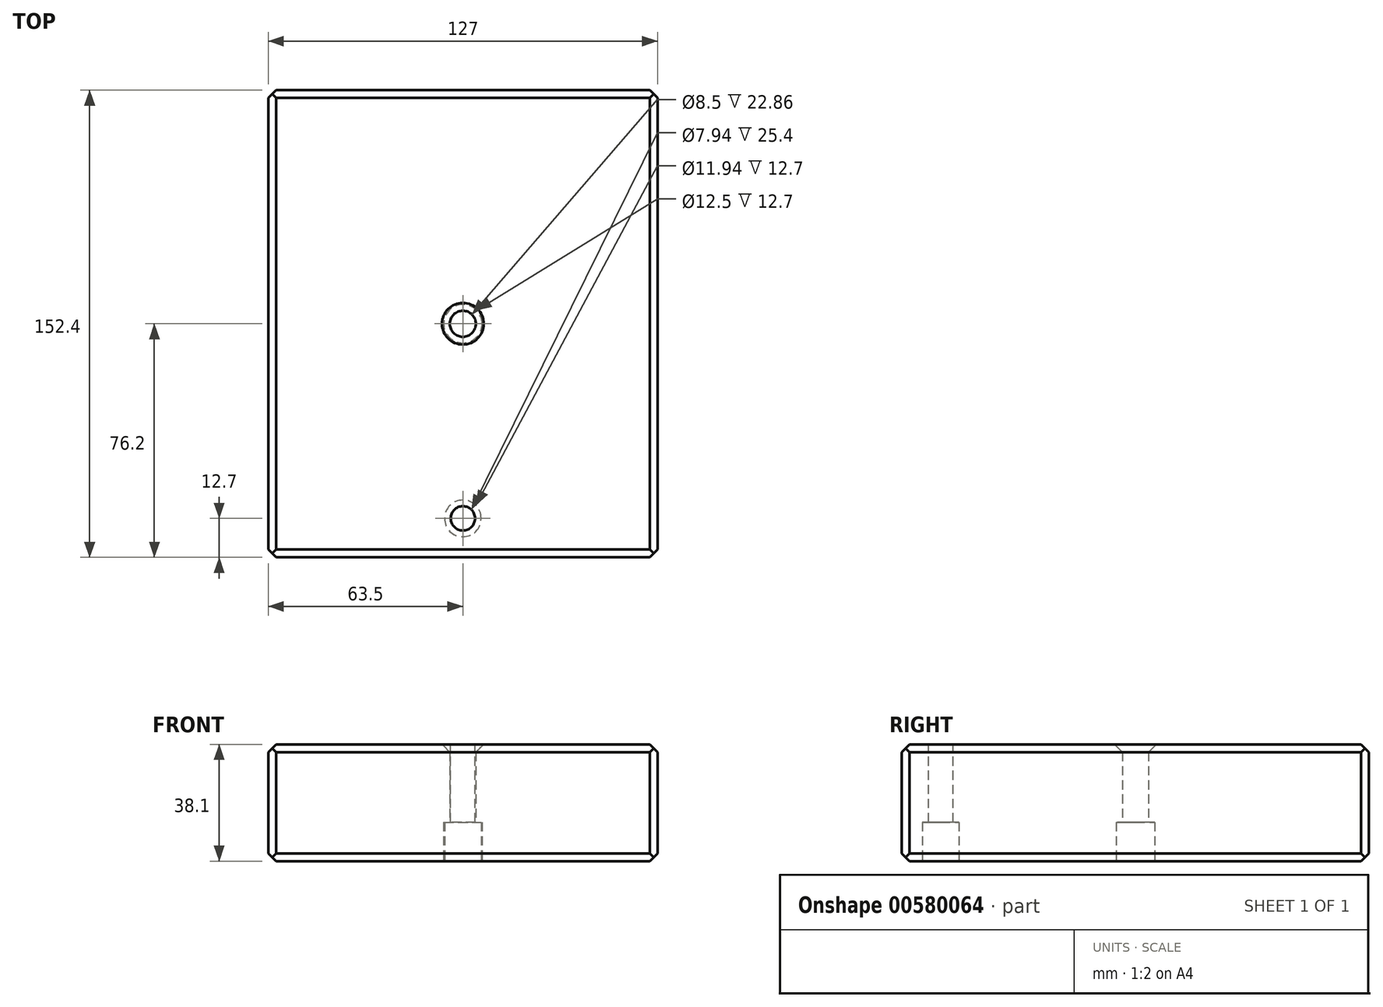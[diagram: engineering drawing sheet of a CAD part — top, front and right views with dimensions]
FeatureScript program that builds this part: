
annotation { "Feature Type Name" : "Feature", "Feature Type Description" : "" }
export const myFeature = defineFeature(function(context is Context, id is Id, definition is map)
    precondition{}
    {
        {
            var Q0;
            Q0=qCreatedBy(makeId("Top.planeOp"),FACE);
            var sketch = newSketch(context, id + "F0", { "sketchPlane" : qUnion([Q0])});
            skLineSegment(sketch, "E0.bottom", {"start": v(63.5, -76.2) * mm, "end": v(-63.5, -76.2) * mm});
            skLineSegment(sketch, "E0.top", {"start": v(63.5, 76.2) * mm, "end": v(-63.5, 76.2) * mm});
            skLineSegment(sketch, "E0.left", {"start": v(63.5, -76.2) * mm, "end": v(63.5, 76.2) * mm});
            skLineSegment(sketch, "E0.right", {"start": v(-63.5, -76.2) * mm, "end": v(-63.5, 76.2) * mm});
            skPoint(sketch, "E0.middle", {"position": v(0, 0) * mm});
            skCircle(sketch, "E1", {"center": v(0, 0) * mm, "radius": 4.25 * mm});
            skSolve(sketch);
        }
        {
            var Q0;
            Q0=makeQuery(id+"F0.imprint","IMPRINT",FACE,{"disambiguationData":[TD([[makeQuery(id+"F0.imprint","IMPRINT",EDGE,{"derivedFrom":sQuery(id+"F0.wireOp",EDGE,"E0.bottom")}),-1.0]])]});
            extrude(context, id + "F1", {"entities" : qUnion([Q0]), "depth" : 38.1 * mm, "offsetDistance" : 25.4 * mm});
        }
        {
            var Q0;
            Q0=makeQuery(id+"F1.opExtrude","CAP_FACE",FACE,{"disambiguationData":[OSD([sQuery(id+"F0.wireOp",EDGE,"E0.bottom"),sQuery(id+"F0.wireOp",EDGE,"E0.top"),sQuery(id+"F0.wireOp",EDGE,"E0.left"),sQuery(id+"F0.wireOp",EDGE,"E0.right"),sQuery(id+"F0.wireOp",EDGE,"E1")])],"isStart":false});
            var sketch = newSketch(context, id + "F2", { "sketchPlane" : qUnion([Q0])});
            skLineSegment(sketch, "E2", {"start": v(0, 94.71) * mm, "end": v(0, -95.69) * mm, "construction": true});
            skPoint(sketch, "E2.startSnap0", {"position": v(0, 76.2) * mm});
            skLineSegment(sketch, "E3", {"start": v(-99.6, 0) * mm, "end": v(96.99, 0) * mm, "construction": true});
            skSolve(sketch);
        }
        {
            var Q0;
            Q0=makeQuery(id+"F2.imprint","IMPRINT",FACE,{"disambiguationData":[TD([[makeQuery(id+"F2.imprint","IMPRINT",EDGE,{"derivedFrom":makeQuery(id+"F1.opExtrude","CAP_EDGE",EDGE,{"disambiguationData":[OSD([sQuery(id+"F0.wireOp",EDGE,"E0.bottom")])],"isStart":false})}),-1.0]])]});
            var sketch = newSketch(context, id + "F3", { "sketchPlane" : qUnion([Q0])});
            skCircle(sketch, "E4", {"center": v(0, -63.5) * mm, "radius": 3.97 * mm});
            skSolve(sketch);
        }
        {
            var Q0;
            Q0=makeQuery(id+"F3.imprint","IMPRINT",FACE,{"disambiguationData":[TD([[makeQuery(id+"F3.imprint","IMPRINT",EDGE,{"derivedFrom":sQuery(id+"F3.wireOp",EDGE,"E4")}),1.0]])]});
            var Q1;
            Q1=makeQuery(id+"F3.imprint","IMPRINT",FACE,{"disambiguationData":[TD([[makeQuery(id+"F3.imprint","IMPRINT",EDGE,{"derivedFrom":sQuery(id+"F3.wireOp",EDGE,"7c92b9c1-a204-463c-bf9a-26367c600006")}),1.0]])]});
            extrude(context, id + "F4", {"entities" : qUnion([Q0, Q1]), "operationType" : NewBodyOperationType.REMOVE, "oppositeDirection" : true, "depth" : 50.8 * mm, "offsetDistance" : 25.4 * mm});
        }
        {
            var Q0;
            Q0=makeQuery(id+"F1.opExtrude","CAP_FACE",FACE,{"disambiguationData":[OSD([sQuery(id+"F0.wireOp",EDGE,"E0.bottom"),sQuery(id+"F0.wireOp",EDGE,"E0.top"),sQuery(id+"F0.wireOp",EDGE,"E0.left"),sQuery(id+"F0.wireOp",EDGE,"E0.right"),sQuery(id+"F0.wireOp",EDGE,"E1")])],"isStart":true});
            var sketch = newSketch(context, id + "F5", { "sketchPlane" : qUnion([Q0])});
            skCircle(sketch, "E5.0", {"center": v(0, 63.5) * mm, "radius": 5.97 * mm});
            skCircle(sketch, "E6.0", {"center": v(0, 0) * mm, "radius": 6.25 * mm});
            skSolve(sketch);
        }
        {
            var Q0;
            Q0=makeQuery(id+"F5.imprint","IMPRINT",FACE,{"disambiguationData":[TD([[makeQuery(id+"F5.imprint","IMPRINT",EDGE,{"derivedFrom":sQuery(id+"F5.wireOp",EDGE,"E6.0")}),1.0]])]});
            var Q1;
            Q1=makeQuery(id+"F5.imprint","IMPRINT",FACE,{"disambiguationData":[TD([[makeQuery(id+"F5.imprint","IMPRINT",EDGE,{"derivedFrom":sQuery(id+"F5.wireOp",EDGE,"E5.0")}),1.0]])]});
            extrude(context, id + "F6", {"entities" : qUnion([Q0, Q1]), "operationType" : NewBodyOperationType.REMOVE, "oppositeDirection" : true, "depth" : 12.7 * mm, "offsetDistance" : 25.4 * mm});
        }
        {
            var Q0;
            Q0=makeQuery(id+"F6.boolean.opBoolean","COPY",EDGE,{"derivedFrom":makeQuery(id+"F6.opExtrude","CAP_EDGE",EDGE,{"disambiguationData":[OSD([sQuery(id+"F5.wireOp",EDGE,"E6.0")])],"isStart":true})});
            var Q1;
            Q1=makeQuery(id+"F4.boolean.opBoolean","INTERSECT",EDGE,{"derivedFrom":[makeQuery(id+"F1.opExtrude","CAP_FACE",FACE,{"disambiguationData":[OSD([sQuery(id+"F0.wireOp",EDGE,"E0.bottom"),sQuery(id+"F0.wireOp",EDGE,"E0.top"),sQuery(id+"F0.wireOp",EDGE,"E0.left"),sQuery(id+"F0.wireOp",EDGE,"E0.right"),sQuery(id+"F0.wireOp",EDGE,"E1")])],"isStart":true}),makeQuery(id+"F4.opExtrude","SWEPT_FACE",FACE,{"disambiguationData":[OSD([sQuery(id+"F3.wireOp",EDGE,"E4")])]})]});
            var Q2;
            Q2=makeQuery(id+"F6.boolean.opBoolean","COPY",EDGE,{"derivedFrom":makeQuery(id+"F6.opExtrude","CAP_EDGE",EDGE,{"disambiguationData":[OSD([sQuery(id+"F5.wireOp",EDGE,"E5.0")])],"isStart":true})});
            var Q3;
            Q3=makeQuery(id+"F4.boolean.opBoolean","COPY",EDGE,{"derivedFrom":makeQuery(id+"F4.opExtrude","CAP_EDGE",EDGE,{"disambiguationData":[OSD([sQuery(id+"F3.wireOp",EDGE,"E4")])],"isStart":true})});
            var Q4;
            Q4=makeQuery(id+"F1.opExtrude","CAP_EDGE",EDGE,{"disambiguationData":[OSD([sQuery(id+"F0.wireOp",EDGE,"E1")])],"isStart":false});
            var Q5;
            Q5=makeQuery(id+"F4.boolean.opBoolean","COPY",EDGE,{"derivedFrom":makeQuery(id+"F4.opExtrude","CAP_EDGE",EDGE,{"disambiguationData":[OSD([sQuery(id+"F3.wireOp",EDGE,"7c92b9c1-a204-463c-bf9a-26367c600006")])],"isStart":true})});
            chamfer(context, id + "F7", {"entities" : qUnion([Q0, Q1, Q2, Q3, Q4, Q5]), "width" : 2.54 * mm, "tangentPropagation" : true});
        }
        {
            var Q0;
            Q0=makeQuery(id+"F1.opExtrude","CAP_EDGE",EDGE,{"disambiguationData":[OSD([sQuery(id+"F0.wireOp",EDGE,"E0.right")])],"isStart":false});
            var Q1;
            Q1=makeQuery(id+"F1.opExtrude","CAP_EDGE",EDGE,{"disambiguationData":[OSD([sQuery(id+"F0.wireOp",EDGE,"E0.bottom")])],"isStart":false});
            var Q2;
            Q2=makeQuery(id+"F1.opExtrude","CAP_EDGE",EDGE,{"disambiguationData":[OSD([sQuery(id+"F0.wireOp",EDGE,"E0.top")])],"isStart":false});
            var Q3;
            Q3=makeQuery(id+"F1.opExtrude","CAP_EDGE",EDGE,{"disambiguationData":[OSD([sQuery(id+"F0.wireOp",EDGE,"E0.left")])],"isStart":false});
            var Q4;
            Q4=makeQuery(id+"F1.opExtrude","CAP_EDGE",EDGE,{"disambiguationData":[OSD([sQuery(id+"F0.wireOp",EDGE,"E0.left")])],"isStart":true});
            var Q5;
            Q5=makeQuery(id+"F1.opExtrude","CAP_EDGE",EDGE,{"disambiguationData":[OSD([sQuery(id+"F0.wireOp",EDGE,"E0.top")])],"isStart":true});
            var Q6;
            Q6=makeQuery(id+"F1.opExtrude","CAP_EDGE",EDGE,{"disambiguationData":[OSD([sQuery(id+"F0.wireOp",EDGE,"E0.right")])],"isStart":true});
            var Q7;
            Q7=makeQuery(id+"F1.opExtrude","CAP_EDGE",EDGE,{"disambiguationData":[OSD([sQuery(id+"F0.wireOp",EDGE,"E0.bottom")])],"isStart":true});
            chamfer(context, id + "F8", {"entities" : qUnion([Q0, Q1, Q2, Q3, Q4, Q5, Q6, Q7]), "width" : 2.54 * mm, "tangentPropagation" : true});
        }
        {
            var Q0;
            Q0=makeQuery(id+"F1.opExtrude","SWEPT_EDGE",EDGE,{"disambiguationData":[OSD([sQuery(id+"F0.wireOp",EDGE,"E0.bottom"),sQuery(id+"F0.wireOp",EDGE,"E0.right")])]});
            var Q1;
            Q1=makeQuery(id+"F1.opExtrude","SWEPT_EDGE",EDGE,{"disambiguationData":[OSD([sQuery(id+"F0.wireOp",EDGE,"E0.bottom"),sQuery(id+"F0.wireOp",EDGE,"E0.left")])]});
            var Q2;
            Q2=makeQuery(id+"F1.opExtrude","SWEPT_EDGE",EDGE,{"disambiguationData":[OSD([sQuery(id+"F0.wireOp",EDGE,"E0.top"),sQuery(id+"F0.wireOp",EDGE,"E0.left")])]});
            var Q3;
            Q3=makeQuery(id+"F1.opExtrude","SWEPT_EDGE",EDGE,{"disambiguationData":[OSD([sQuery(id+"F0.wireOp",EDGE,"E0.top"),sQuery(id+"F0.wireOp",EDGE,"E0.right")])]});
            chamfer(context, id + "F9", {"entities" : qUnion([Q0, Q1, Q2, Q3]), "width" : 2.54 * mm, "tangentPropagation" : true});
        }
    });
